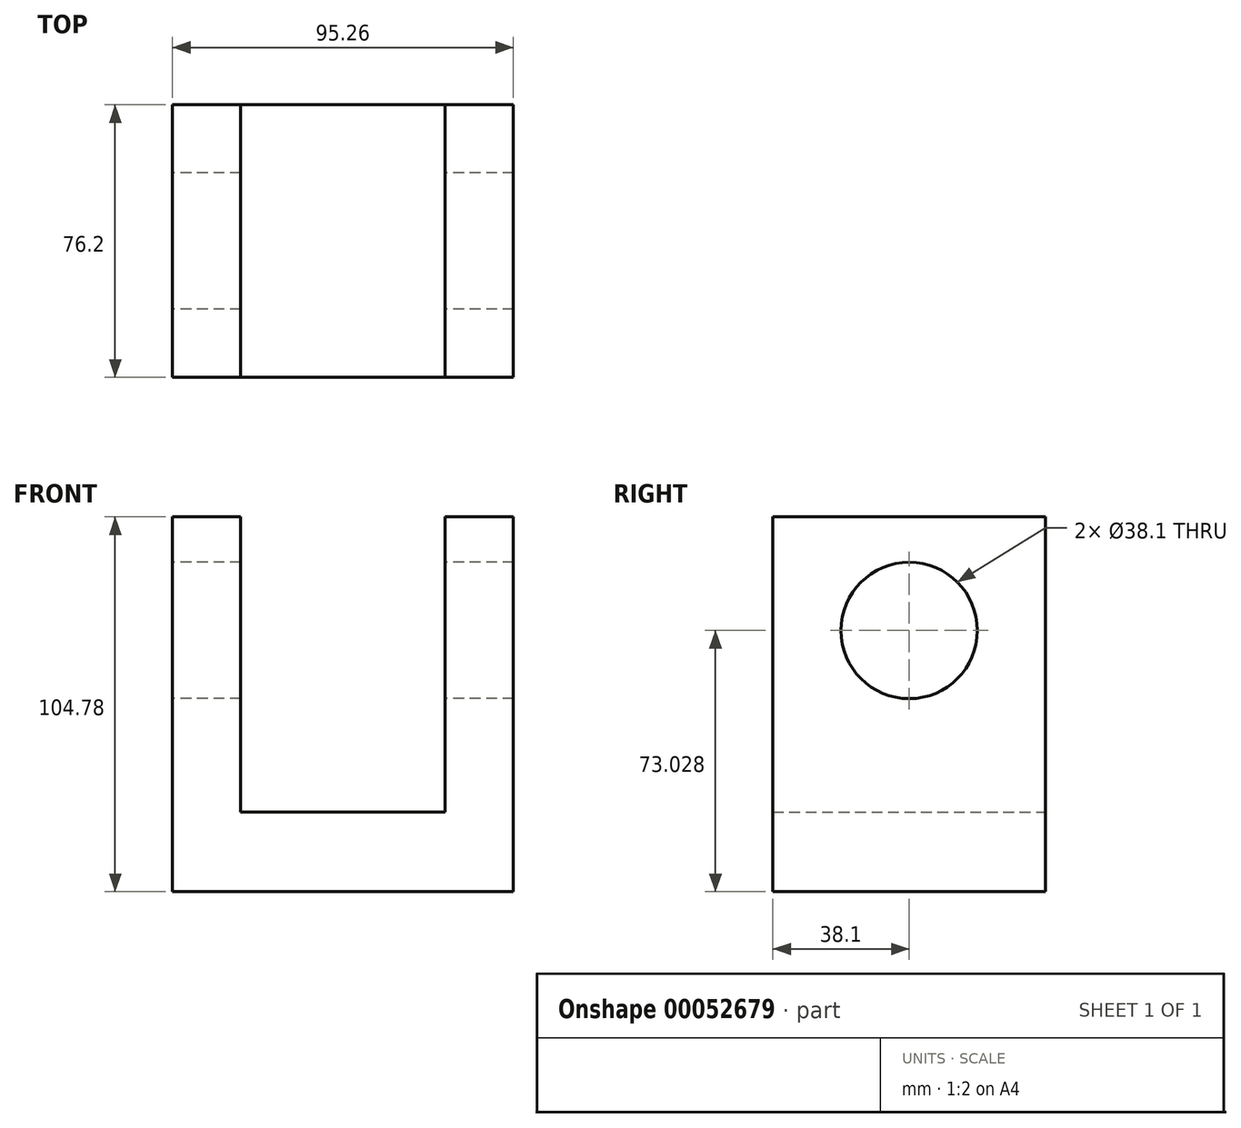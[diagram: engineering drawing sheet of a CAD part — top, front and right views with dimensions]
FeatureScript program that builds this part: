
annotation { "Feature Type Name" : "Feature", "Feature Type Description" : "" }
export const myFeature = defineFeature(function(context is Context, id is Id, definition is map)
    precondition{}
    {
        {
            var Q0;
            Q0=qCreatedBy(makeId("Front.planeOp"),FACE);
            var sketch = newSketch(context, id + "F0", { "sketchPlane" : qUnion([Q0])});
            skLineSegment(sketch, "E0.bottom", {"start": v(-47.62, -52.39) * mm, "end": v(47.63, -52.39) * mm});
            skLineSegment(sketch, "E0.top", {"start": v(-47.63, 52.39) * mm, "end": v(47.62, 52.39) * mm});
            skLineSegment(sketch, "E0.left", {"start": v(-47.62, -52.39) * mm, "end": v(-47.63, 52.39) * mm});
            skLineSegment(sketch, "E0.right", {"start": v(47.63, -52.39) * mm, "end": v(47.62, 52.39) * mm});
            skPoint(sketch, "E0.middle", {"position": v(0, 0) * mm});
            skLineSegment(sketch, "E1", {"start": v(-28.58, 52.39) * mm, "end": v(-28.58, -30.16) * mm});
            skLineSegment(sketch, "E2", {"start": v(-28.58, -30.16) * mm, "end": v(28.58, -30.16) * mm});
            skLineSegment(sketch, "E3", {"start": v(28.58, -30.16) * mm, "end": v(28.57, 52.39) * mm});
            skSolve(sketch);
        }
        {
            var Q0;
            Q0=makeQuery(id+"F0.imprint","IMPRINT",FACE,{"disambiguationData":[TD([[makeQuery(id+"F0.imprint","IMPRINT",EDGE,{"derivedFrom":sQuery(id+"F0.wireOp",EDGE,"E0.bottom")}),1.0]])]});
            extrude(context, id + "F1", {"entities" : qUnion([Q0]), "depth" : 76.2 * mm, "offsetDistance" : 25.4 * mm});
        }
        {
            var Q0;
            Q0=makeQuery(id+"F1.opExtrude","SWEPT_FACE",FACE,{"disambiguationData":[OSD([sQuery(id+"F0.wireOp",EDGE,"E0.left")])]});
            var sketch = newSketch(context, id + "F2", { "sketchPlane" : qUnion([Q0])});
            skLineSegment(sketch, "E4.0.0", {"start": v(0, 52.39) * mm, "end": v(0, -52.39) * mm});
            skLineSegment(sketch, "E4.0.1", {"start": v(0, -52.39) * mm, "end": v(76.2, -52.39) * mm});
            skLineSegment(sketch, "E4.0.2", {"start": v(76.2, -52.39) * mm, "end": v(76.2, 52.39) * mm});
            skLineSegment(sketch, "E4.0.3", {"start": v(76.2, 52.39) * mm, "end": v(0, 52.39) * mm});
            skPoint(sketch, "E5", {"position": v(38.1, 20.64) * mm});
            skPoint(sketch, "E5.positionSnap0", {"position": v(38.1, 52.39) * mm});
            skSolve(sketch);
        }
        {
            var Q0;
            Q0=sQuery(id+"F2.wireOp",VERTEX,"E5");
            var Q1;
            Q1=makeQuery(id+"F1.opExtrude","SWEPT_BODY",BODY,{"disambiguationData":[OSD([sQuery(id+"F0.wireOp",EDGE,"E0.bottom"),sQuery(id+"F0.wireOp",EDGE,"E0.top"),sQuery(id+"F0.wireOp",EDGE,"E0.left"),sQuery(id+"F0.wireOp",EDGE,"E0.right"),sQuery(id+"F0.wireOp",EDGE,"E1"),sQuery(id+"F0.wireOp",EDGE,"E2"),sQuery(id+"F0.wireOp",EDGE,"E3")])]});
            hole(context, id + "F3", {"style" : HoleStyle.SIMPLE, "endStyle" : HoleEndStyle.THROUGH, "holeDiameter" : 38.1 * mm, "majorDiameter" : 6.35 * mm, "isTappedThrough" : true, "tappedDepth" : 15.88 * mm, "tapClearance" : 3, "locations" : qUnion([Q0]), "scope" : qUnion([Q1])});
        }
    });
